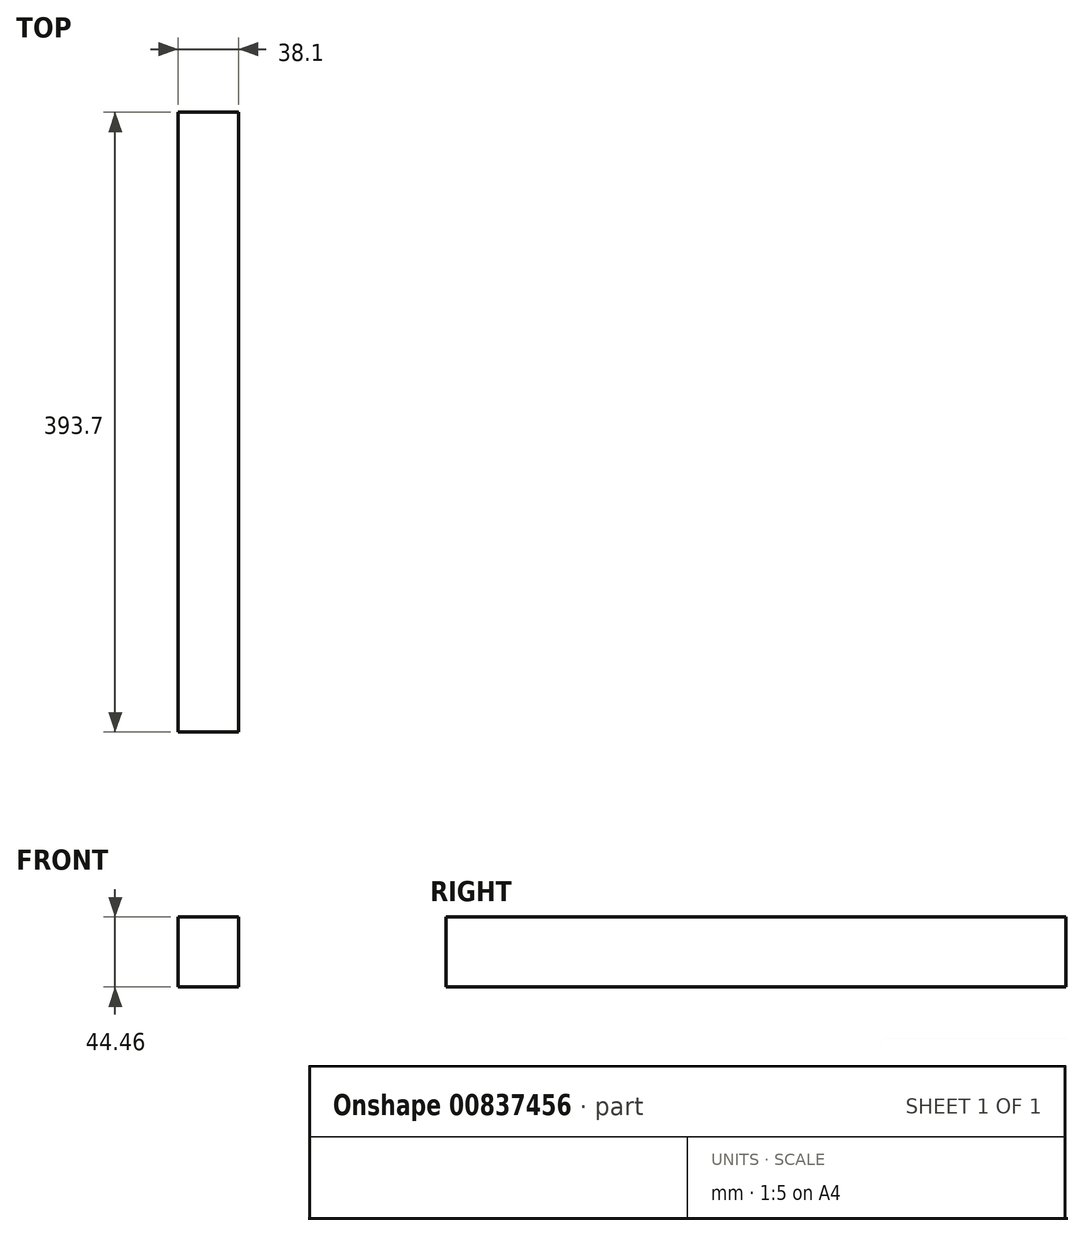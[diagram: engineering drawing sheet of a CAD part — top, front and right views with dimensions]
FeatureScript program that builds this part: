
annotation { "Feature Type Name" : "Feature", "Feature Type Description" : "" }
export const myFeature = defineFeature(function(context is Context, id is Id, definition is map)
    precondition{}
    {
        {
            var Q0;
            Q0=qCreatedBy(makeId("Front.planeOp"),FACE);
            var sketch = newSketch(context, id + "F0", { "sketchPlane" : qUnion([Q0])});
            skLineSegment(sketch, "E0.bottom", {"start": v(19.05, 22.23) * mm, "end": v(-19.05, 22.23) * mm});
            skLineSegment(sketch, "E0.top", {"start": v(19.05, -22.23) * mm, "end": v(-19.05, -22.23) * mm});
            skLineSegment(sketch, "E0.left", {"start": v(19.05, 22.23) * mm, "end": v(19.05, -22.23) * mm});
            skLineSegment(sketch, "E0.right", {"start": v(-19.05, 22.23) * mm, "end": v(-19.05, -22.23) * mm});
            skPoint(sketch, "E0.middle", {"position": v(0, 0) * mm});
            skSolve(sketch);
        }
        {
            var Q0;
            Q0=makeQuery(id+"F0.imprint","IMPRINT",FACE,{"disambiguationData":[TD([[makeQuery(id+"F0.imprint","IMPRINT",EDGE,{"derivedFrom":sQuery(id+"F0.wireOp",EDGE,"E0.bottom")}),1.0]])]});
            extrude(context, id + "F1", {"entities" : qUnion([Q0]), "endBound" : BoundingType.SYMMETRIC, "depth" : 393.7 * mm, "offsetDistance" : 25.4 * mm});
        }
    });
